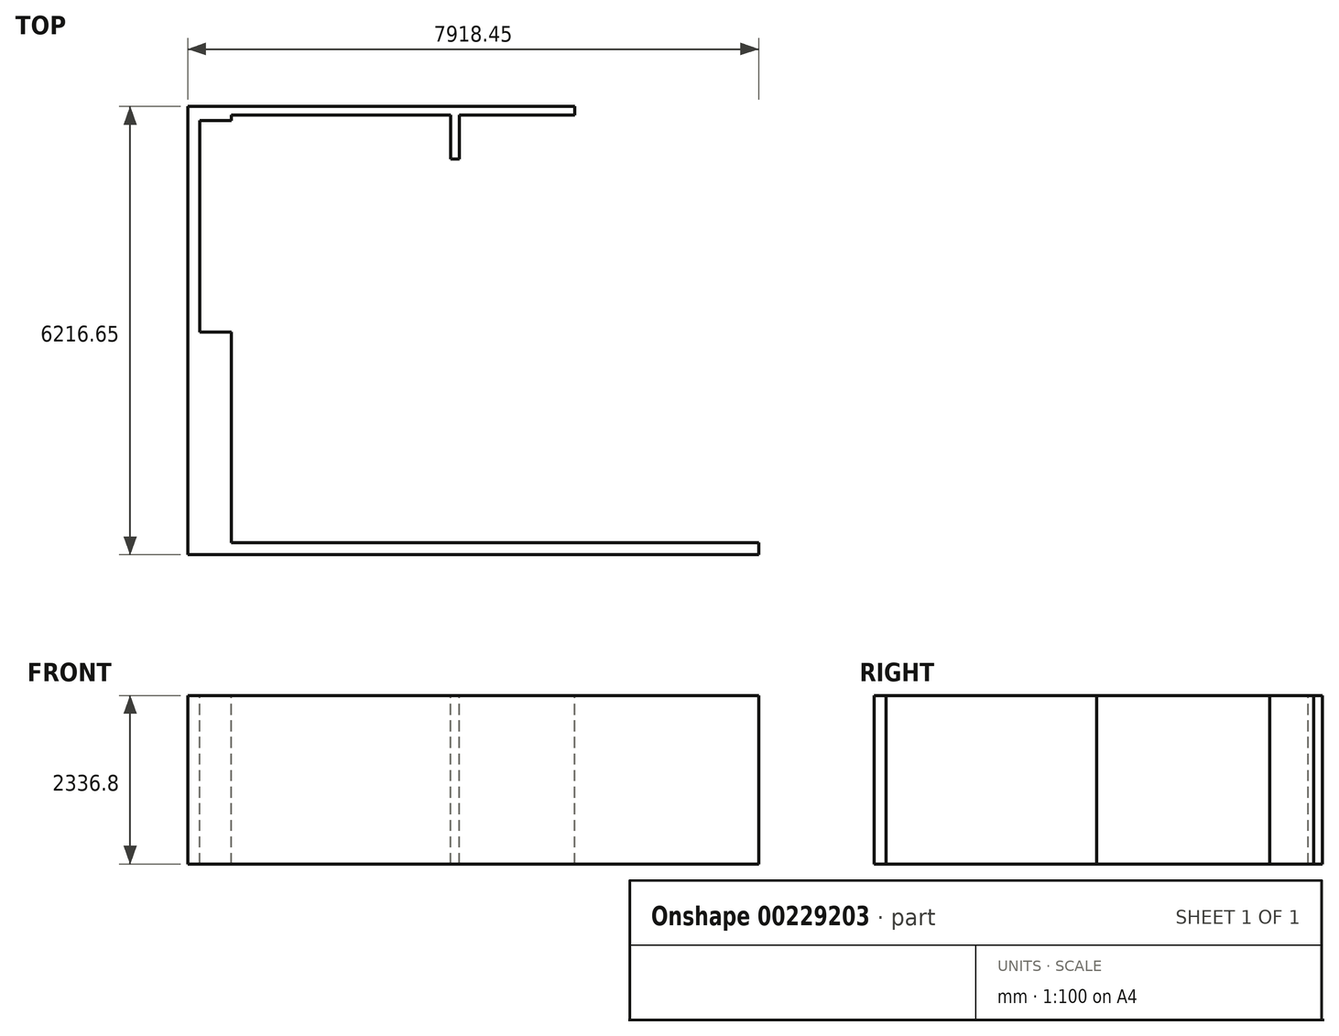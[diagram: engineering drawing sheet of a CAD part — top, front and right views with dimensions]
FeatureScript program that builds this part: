
annotation { "Feature Type Name" : "Feature", "Feature Type Description" : "" }
export const myFeature = defineFeature(function(context is Context, id is Id, definition is map)
    precondition{}
    {
        {
            var Q0;
            Q0=qCreatedBy(makeId("Top.planeOp"),FACE);
            var sketch = newSketch(context, id + "F0", { "sketchPlane" : qUnion([Q0])});
            skLineSegment(sketch, "E0", {"start": v(0, 0) * mm, "end": v(0, 2921) * mm});
            skLineSegment(sketch, "E1", {"start": v(0, 2921) * mm, "end": v(-438.15, 2921) * mm});
            skLineSegment(sketch, "E2", {"start": v(-438.15, 2921) * mm, "end": v(-438.15, 5854.7) * mm});
            skLineSegment(sketch, "E3", {"start": v(-438.15, 5854.7) * mm, "end": v(0, 5854.7) * mm});
            skLineSegment(sketch, "E4", {"start": v(0, 5854.7) * mm, "end": v(0, 5930.9) * mm});
            skLineSegment(sketch, "E5", {"start": v(0, 5930.9) * mm, "end": v(3041.65, 5930.9) * mm});
            skLineSegment(sketch, "E6", {"start": v(3041.65, 5930.9) * mm, "end": v(3041.65, 5321.3) * mm});
            skLineSegment(sketch, "E7", {"start": v(3041.65, 5321.3) * mm, "end": v(3162.3, 5321.3) * mm});
            skLineSegment(sketch, "E8", {"start": v(3162.3, 5321.3) * mm, "end": v(3162.3, 5930.9) * mm});
            skLineSegment(sketch, "E9", {"start": v(3162.3, 5930.9) * mm, "end": v(4762.5, 5930.9) * mm});
            skLineSegment(sketch, "E10", {"start": v(4762.5, 5930.9) * mm, "end": v(4762.5, 6051.55) * mm});
            skLineSegment(sketch, "E11", {"start": v(4762.5, 6051.55) * mm, "end": v(0, 6051.55) * mm});
            skLineSegment(sketch, "E12", {"start": v(0, 6051.55) * mm, "end": v(-603.25, 6051.55) * mm});
            skLineSegment(sketch, "E13", {"start": v(-603.25, 6051.55) * mm, "end": v(-603.25, -165.1) * mm});
            skLineSegment(sketch, "E14", {"start": v(-603.25, -165.1) * mm, "end": v(7315.2, -165.1) * mm});
            skLineSegment(sketch, "E15", {"start": v(7315.2, -165.1) * mm, "end": v(7315.2, 0) * mm});
            skLineSegment(sketch, "E16", {"start": v(7315.2, 0) * mm, "end": v(0, 0) * mm});
            skSolve(sketch);
        }
        {
            var Q0;
            Q0=makeQuery(id+"F0.imprint","IMPRINT",FACE,{"disambiguationData":[TD([[makeQuery(id+"F0.imprint","IMPRINT",EDGE,{"derivedFrom":sQuery(id+"F0.wireOp",EDGE,"E0")}),1.0]])]});
            extrude(context, id + "F1", {"entities" : qUnion([Q0]), "oppositeDirection" : true, "depth" : 2336.8 * mm});
        }
    });
